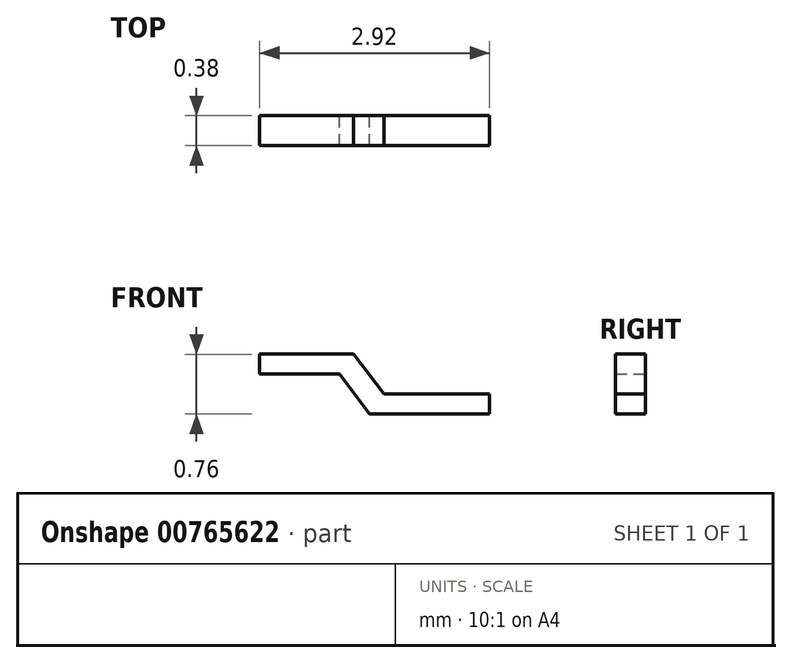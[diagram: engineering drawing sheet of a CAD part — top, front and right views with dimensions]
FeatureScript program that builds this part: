
annotation { "Feature Type Name" : "Feature", "Feature Type Description" : "" }
export const myFeature = defineFeature(function(context is Context, id is Id, definition is map)
    precondition{}
    {
        {
            var Q0;
            Q0=qCreatedBy(makeId("Front.planeOp"),FACE);
            var sketch = newSketch(context, id + "F0", { "sketchPlane" : qUnion([Q0])});
            skLineSegment(sketch, "E0", {"start": v(0, 0.5) * mm, "end": v(1.02, 0.5) * mm});
            skLineSegment(sketch, "E1", {"start": v(1.02, 0.5) * mm, "end": v(1.4, 0) * mm});
            skLineSegment(sketch, "E2", {"start": v(1.4, 0) * mm, "end": v(2.92, 0) * mm});
            skLineSegment(sketch, "E3", {"start": v(2.92, 0) * mm, "end": v(2.92, 0.25) * mm});
            skLineSegment(sketch, "E4", {"start": v(2.92, 0.25) * mm, "end": v(1.58, 0.25) * mm});
            skLineSegment(sketch, "E5", {"start": v(1.58, 0.25) * mm, "end": v(1.2, 0.76) * mm});
            skLineSegment(sketch, "E6", {"start": v(1.2, 0.76) * mm, "end": v(0, 0.76) * mm});
            skLineSegment(sketch, "E7", {"start": v(0, 0.76) * mm, "end": v(0, 0.5) * mm});
            skLineSegment(sketch, "E8", {"start": v(0, 0.76) * mm, "end": v(0, 0) * mm});
            skSolve(sketch);
        }
        {
            var Q0;
            Q0=makeQuery(id+"F0.imprint","IMPRINT",FACE,{"disambiguationData":[TD([[makeQuery(id+"F0.imprint","IMPRINT",EDGE,{"derivedFrom":sQuery(id+"F0.wireOp",EDGE,"E0")}),1.0]])]});
            extrude(context, id + "F1", {"entities" : qUnion([Q0]), "depth" : 0.38 * mm, "offsetDistance" : 25.4 * mm});
        }
    });
